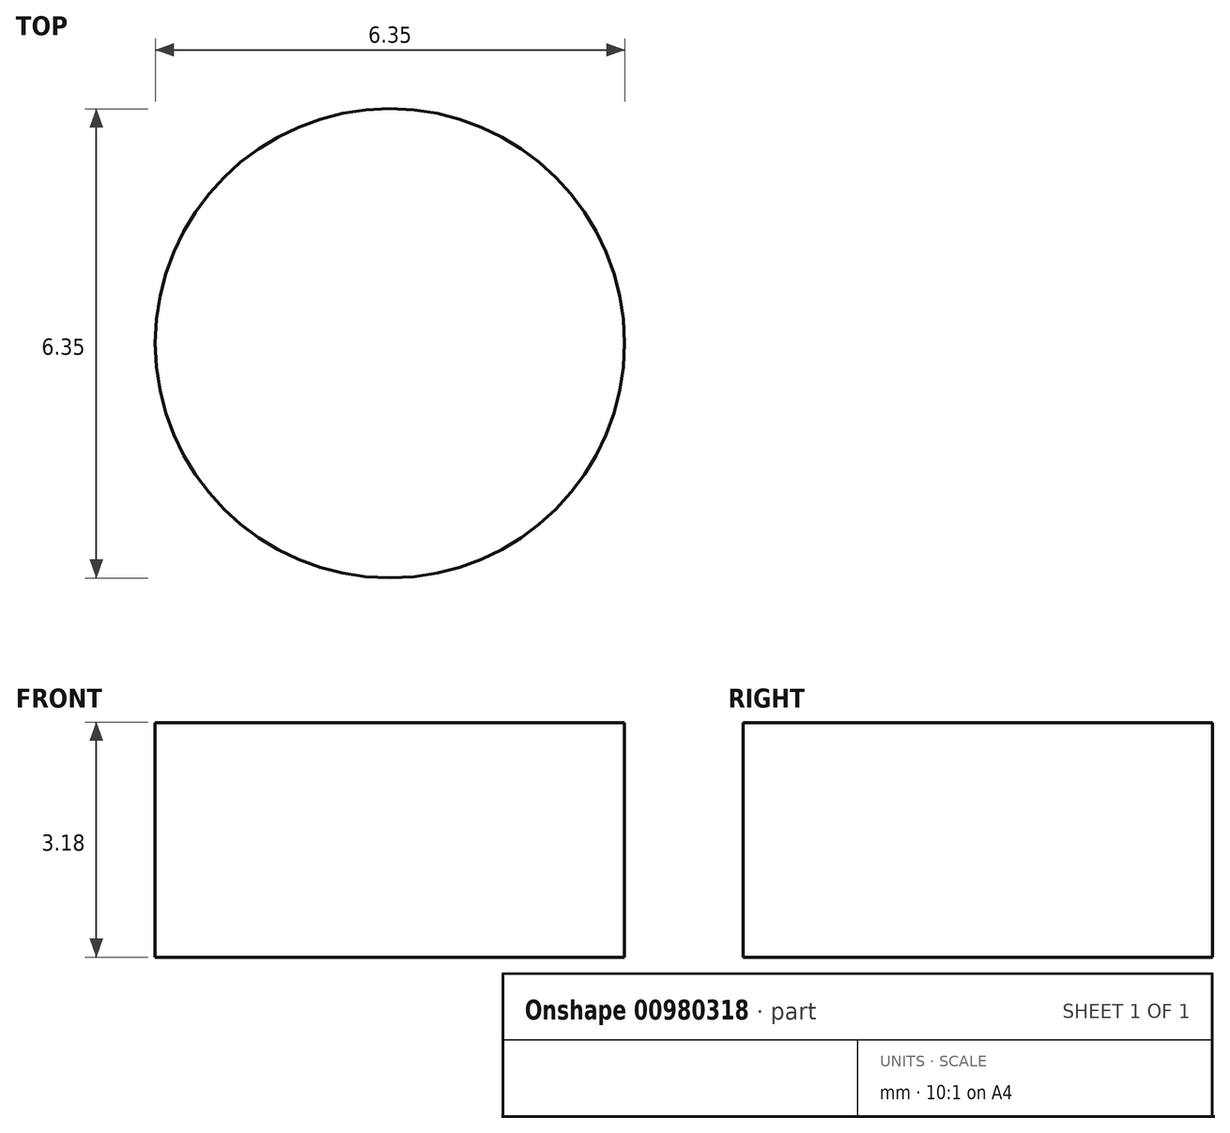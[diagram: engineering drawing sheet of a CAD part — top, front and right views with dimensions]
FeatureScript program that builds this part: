
annotation { "Feature Type Name" : "Feature", "Feature Type Description" : "" }
export const myFeature = defineFeature(function(context is Context, id is Id, definition is map)
    precondition{}
    {
        {
            var Q0;
            Q0=qCreatedBy(makeId("Top.planeOp"),FACE);
            var sketch = newSketch(context, id + "F0", { "sketchPlane" : qUnion([Q0])});
            skCircle(sketch, "E0", {"center": v(-56.04, 29.72) * mm, "radius": 3.18 * mm});
            skSolve(sketch);
        }
        {
            var Q0;
            Q0 = qSketchRegion(id + "F0", true);
            extrude(context, id + "F1", {"entities" : qUnion([Q0]), "depth" : 3.17 * mm, "offsetDistance" : 25.4 * mm});
        }
    });
